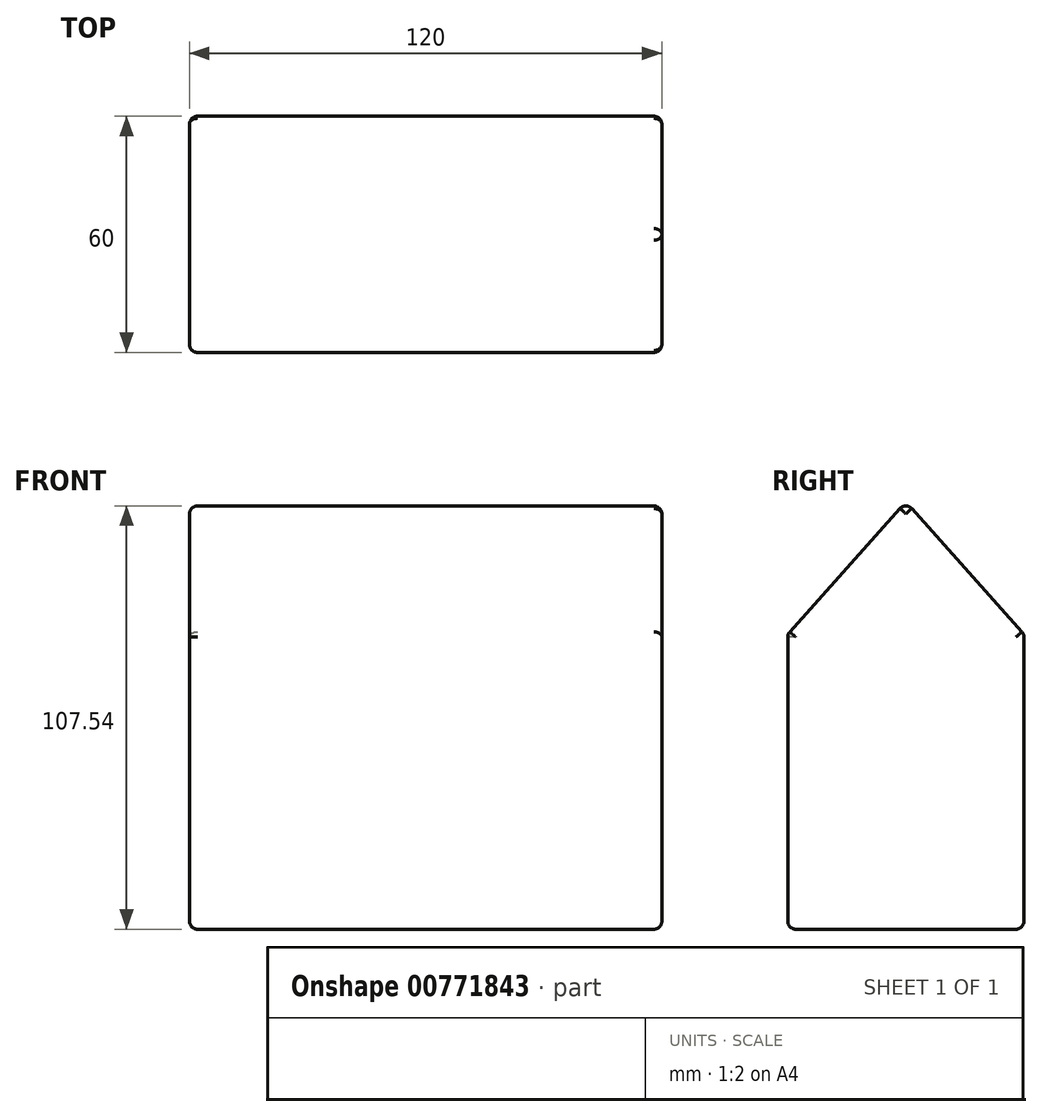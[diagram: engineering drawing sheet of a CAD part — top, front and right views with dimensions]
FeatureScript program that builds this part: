
annotation { "Feature Type Name" : "Feature", "Feature Type Description" : "" }
export const myFeature = defineFeature(function(context is Context, id is Id, definition is map)
    precondition{}
    {
        {
            var Q0;
            Q0=qCreatedBy(makeId("Front.planeOp"),FACE);
            var sketch = newSketch(context, id + "F0", { "sketchPlane" : qUnion([Q0])});
            skLineSegment(sketch, "E0.bottom", {"start": v(60, -37.5) * mm, "end": v(-60, -37.5) * mm});
            skLineSegment(sketch, "E0.top", {"start": v(60, 37.5) * mm, "end": v(-60, 37.5) * mm});
            skLineSegment(sketch, "E0.left", {"start": v(60, -37.5) * mm, "end": v(60, 37.5) * mm});
            skLineSegment(sketch, "E0.right", {"start": v(-60, -37.5) * mm, "end": v(-60, 37.5) * mm});
            skPoint(sketch, "E0.middle", {"position": v(0, 0) * mm});
            skSolve(sketch);
        }
        {
            var Q0;
            Q0 = qSketchRegion(id + "F0", true);
            extrude(context, id + "F1", {"entities" : qUnion([Q0]), "endBound" : BoundingType.SYMMETRIC, "depth" : 60 * mm, "offsetDistance" : 25 * mm});
        }
        {
            var Q0;
            Q0=makeQuery(id+"F1.opExtrude","SWEPT_FACE",FACE,{"disambiguationData":[OSD([sQuery(id+"F0.wireOp",EDGE,"E0.right")])]});
            var sketch = newSketch(context, id + "F2", { "sketchPlane" : qUnion([Q0])});
            skLineSegment(sketch, "E1", {"start": v(-30, 37.5) * mm, "end": v(0, 71.04) * mm});
            skLineSegment(sketch, "E2", {"start": v(0, 71.04) * mm, "end": v(30, 37.5) * mm});
            skSolve(sketch);
        }
        {
            var Q0;
            Q0=makeQuery(id+"F2.imprint","IMPRINT",FACE,{"disambiguationData":[TD([[makeQuery(id+"F2.imprint","IMPRINT",EDGE,{"derivedFrom":sQuery(id+"F2.wireOp",EDGE,"E1")}),-1.0]])]});
            extrude(context, id + "F3", {"entities" : qUnion([Q0]), "operationType" : NewBodyOperationType.ADD, "oppositeDirection" : true, "depth" : 120 * mm, "offsetDistance" : 25 * mm});
        }
        {
            var Q0;
            Q0=makeQuery(id+"F1.opExtrude","CAP_EDGE",EDGE,{"disambiguationData":[OSD([sQuery(id+"F0.wireOp",EDGE,"E0.right")])],"isStart":false});
            fillet(context, id + "F4", {"entities" : qUnion([Q0]), "radius" : 2 * mm, "tangentPropagation" : true, "allowEdgeOverflow" : false});
        }
        {
            var Q0;
            Q0=makeQuery(id+"F1.opExtrude","CAP_EDGE",EDGE,{"disambiguationData":[OSD([sQuery(id+"F0.wireOp",EDGE,"E0.left")])],"isStart":false});
            var Q1;
            Q1=makeQuery(id+"F1.opExtrude","CAP_EDGE",EDGE,{"disambiguationData":[OSD([sQuery(id+"F0.wireOp",EDGE,"E0.bottom")])],"isStart":false});
            var Q2;
            Q2=makeQuery(id+"F3.opExtrude","SWEPT_EDGE",EDGE,{"disambiguationData":[OSD([sQuery(id+"F2.wireOp",EDGE,"E1"),sQuery(id+"F2.wireOp",EDGE,"E2")])]});
            var Q3;
            Q3=makeQuery(id+"F3.opExtrude","CAP_EDGE",EDGE,{"disambiguationData":[OSD([sQuery(id+"F2.wireOp",EDGE,"E2")])],"isStart":false});
            var Q4;
            Q4=makeQuery(id+"F1.opExtrude","CAP_EDGE",EDGE,{"disambiguationData":[OSD([sQuery(id+"F0.wireOp",EDGE,"E0.left")])],"isStart":true});
            var Q5;
            Q5=makeQuery(id+"F1.opExtrude","SWEPT_EDGE",EDGE,{"disambiguationData":[OSD([sQuery(id+"F0.wireOp",EDGE,"E0.bottom"),sQuery(id+"F0.wireOp",EDGE,"E0.left")])]});
            var Q6;
            {var subQ0=sQuery(id+"F0.wireOp",EDGE,"E0.top");Q6=makeQuery(id+"F3.boolean.opBoolean","MERGE",EDGE,{"derivedFrom":[makeQuery(id+"F1.opExtrude","CAP_EDGE",EDGE,{"disambiguationData":[OSD([subQ0])],"isStart":true}),makeQuery(id+"F3.opExtrude","SWEPT_EDGE",EDGE,{"disambiguationData":[OSD([subQ0,sQuery(id+"F0.wireOp",EDGE,"E0.right"),sQuery(id+"F2.wireOp",EDGE,"E1")])]})]});}
            var Q7;
            Q7=makeQuery(id+"F1.opExtrude","CAP_EDGE",EDGE,{"disambiguationData":[OSD([sQuery(id+"F0.wireOp",EDGE,"E0.bottom")])],"isStart":true});
            var Q8;
            Q8=makeQuery(id+"F1.opExtrude","CAP_EDGE",EDGE,{"disambiguationData":[OSD([sQuery(id+"F0.wireOp",EDGE,"E0.right")])],"isStart":true});
            fillet(context, id + "F5", {"entities" : qUnion([Q0, Q1, Q2, Q3, Q4, Q5, Q6, Q7, Q8]), "radius" : 2 * mm, "tangentPropagation" : true, "allowEdgeOverflow" : false});
        }
        {
            var Q0;
            Q0=makeQuery(id+"F3.opExtrude","CAP_EDGE",EDGE,{"disambiguationData":[OSD([sQuery(id+"F2.wireOp",EDGE,"E1")])],"isStart":false});
            fillet(context, id + "F6", {"entities" : qUnion([Q0]), "radius" : 2 * mm, "tangentPropagation" : true, "allowEdgeOverflow" : false});
        }
        {
            var Q0;
            Q0=makeQuery(id+"F3.opExtrude","CAP_EDGE",EDGE,{"disambiguationData":[OSD([sQuery(id+"F2.wireOp",EDGE,"E1")])],"isStart":true});
            fillet(context, id + "F7", {"entities" : qUnion([Q0]), "radius" : 2 * mm, "tangentPropagation" : true, "allowEdgeOverflow" : false});
        }
    });
